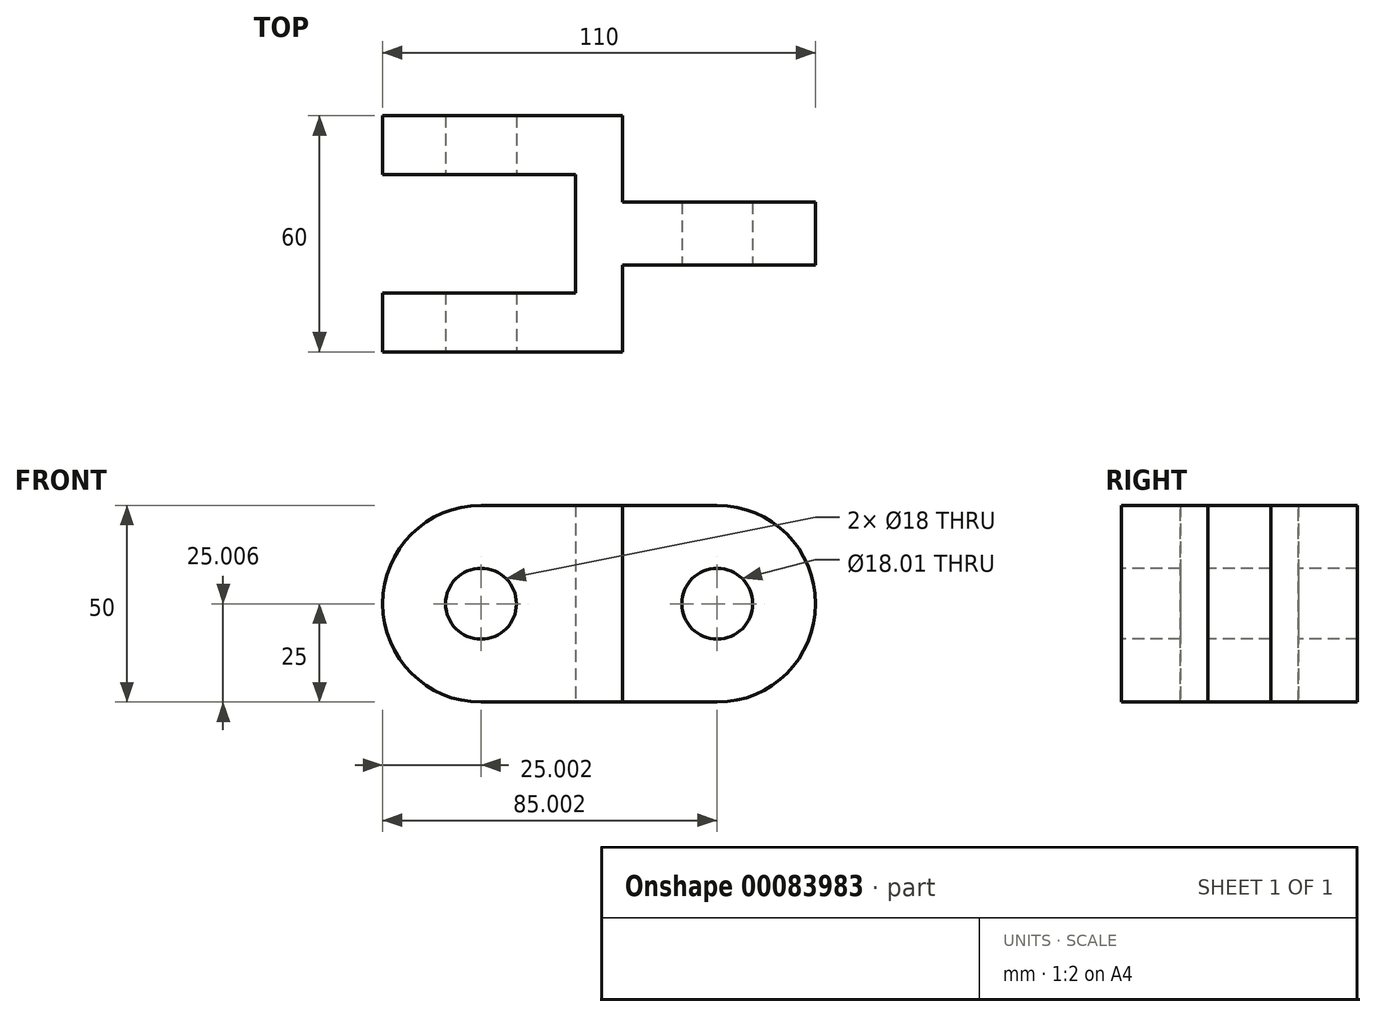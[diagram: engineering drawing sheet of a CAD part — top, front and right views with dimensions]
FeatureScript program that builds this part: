
annotation { "Feature Type Name" : "Feature", "Feature Type Description" : "" }
export const myFeature = defineFeature(function(context is Context, id is Id, definition is map)
    precondition{}
    {
        {
            var Q0;
            Q0=qCreatedBy(makeId("Top.planeOp"),FACE);
            var sketch = newSketch(context, id + "F0", { "sketchPlane" : qUnion([Q0])});
            skLineSegment(sketch, "E0.bottom", {"start": v(-55.44, 42.33) * mm, "end": v(54.56, 42.33) * mm});
            skLineSegment(sketch, "E0.top", {"start": v(-55.44, -17.67) * mm, "end": v(54.56, -17.67) * mm});
            skLineSegment(sketch, "E0.left", {"start": v(-55.44, 42.33) * mm, "end": v(-55.44, -17.67) * mm});
            skLineSegment(sketch, "E0.right", {"start": v(54.56, 42.33) * mm, "end": v(54.56, -17.67) * mm});
            skSolve(sketch);
        }
        {
            var Q0;
            Q0 = qSketchRegion(id + "F0", true);
            extrude(context, id + "F1", {"entities" : qUnion([Q0]), "depth" : 50 * mm});
        }
        {
            var Q0;
            Q0=qCreatedBy(makeId("Top.planeOp"),FACE);
            var sketch = newSketch(context, id + "F2", { "sketchPlane" : qUnion([Q0])});
            skLineSegment(sketch, "E1.bottom", {"start": v(54.56, -17.67) * mm, "end": v(5.56, -17.67) * mm});
            skLineSegment(sketch, "E1.top", {"start": v(54.56, 4.33) * mm, "end": v(5.56, 4.33) * mm});
            skLineSegment(sketch, "E1.left", {"start": v(54.56, -17.67) * mm, "end": v(54.56, 4.33) * mm});
            skLineSegment(sketch, "E1.right", {"start": v(5.56, -17.67) * mm, "end": v(5.56, 4.33) * mm});
            skLineSegment(sketch, "E2.bottom", {"start": v(54.56, 42.33) * mm, "end": v(5.57, 42.33) * mm});
            skLineSegment(sketch, "E2.top", {"start": v(54.56, 20.33) * mm, "end": v(5.57, 20.33) * mm});
            skLineSegment(sketch, "E2.left", {"start": v(54.56, 42.33) * mm, "end": v(54.56, 20.33) * mm});
            skLineSegment(sketch, "E2.right", {"start": v(5.57, 42.33) * mm, "end": v(5.57, 20.33) * mm});
            skLineSegment(sketch, "E3.bottom", {"start": v(-55.44, 27.33) * mm, "end": v(-6.44, 27.33) * mm});
            skLineSegment(sketch, "E3.top", {"start": v(-55.44, -2.67) * mm, "end": v(-6.44, -2.67) * mm});
            skLineSegment(sketch, "E3.left", {"start": v(-55.44, 27.33) * mm, "end": v(-55.44, -2.67) * mm});
            skLineSegment(sketch, "E3.right", {"start": v(-6.44, 27.33) * mm, "end": v(-6.44, -2.67) * mm});
            skSolve(sketch);
        }
        {
            var Q0;
            Q0 = qSketchRegion(id + "F2", true);
            extrude(context, id + "F3", {"entities" : qUnion([Q0]), "operationType" : NewBodyOperationType.REMOVE, "depth" : 50 * mm});
        }
        {
            var Q0;
            {var subQ0=sQuery(id+"F0.wireOp",EDGE,"E0.bottom");var subQ1=sQuery(id+"F0.wireOp",EDGE,"E0.left");Q0=makeQuery(id+"F3.boolean.opBoolean","SPLIT",EDGE,{"disambiguationData":[TD([makeQuery(id+"F1.opExtrude","SWEPT_FACE",FACE,{"disambiguationData":[OSD([subQ0])]})])],"derivedFrom":makeQuery(id+"F1.opExtrude","CAP_EDGE",EDGE,{"disambiguationData":[OSD([subQ1])],"isStart":false})});}
            var Q1;
            {var subQ0=sQuery(id+"F0.wireOp",EDGE,"E0.bottom");var subQ1=sQuery(id+"F0.wireOp",EDGE,"E0.left");Q1=makeQuery(id+"F3.boolean.opBoolean","SPLIT",EDGE,{"disambiguationData":[TD([makeQuery(id+"F1.opExtrude","SWEPT_FACE",FACE,{"disambiguationData":[OSD([subQ0])]})])],"derivedFrom":makeQuery(id+"F1.opExtrude","CAP_EDGE",EDGE,{"disambiguationData":[OSD([subQ1])],"isStart":true})});}
            var Q2;
            {var subQ0=sQuery(id+"F0.wireOp",EDGE,"E0.left");var subQ1=sQuery(id+"F0.wireOp",EDGE,"E0.top");Q2=makeQuery(id+"F3.boolean.opBoolean","SPLIT",EDGE,{"disambiguationData":[TD([makeQuery(id+"F1.opExtrude","SWEPT_FACE",FACE,{"disambiguationData":[OSD([subQ1])]})])],"derivedFrom":makeQuery(id+"F1.opExtrude","CAP_EDGE",EDGE,{"disambiguationData":[OSD([subQ0])],"isStart":false})});}
            var Q3;
            {var subQ0=sQuery(id+"F0.wireOp",EDGE,"E0.left");var subQ1=sQuery(id+"F0.wireOp",EDGE,"E0.top");Q3=makeQuery(id+"F3.boolean.opBoolean","SPLIT",EDGE,{"disambiguationData":[TD([makeQuery(id+"F1.opExtrude","SWEPT_FACE",FACE,{"disambiguationData":[OSD([subQ1])]})])],"derivedFrom":makeQuery(id+"F1.opExtrude","CAP_EDGE",EDGE,{"disambiguationData":[OSD([subQ0])],"isStart":true})});}
            var Q4;
            Q4=makeQuery(id+"F1.opExtrude","CAP_EDGE",EDGE,{"disambiguationData":[OSD([sQuery(id+"F0.wireOp",EDGE,"E0.right")])],"isStart":false});
            var Q5;
            Q5=makeQuery(id+"F1.opExtrude","CAP_EDGE",EDGE,{"disambiguationData":[OSD([sQuery(id+"F0.wireOp",EDGE,"E0.right")])],"isStart":true});
            fillet(context, id + "F4", {"entities" : qUnion([Q0, Q1, Q2, Q3, Q4, Q5]), "radius" : 25 * mm, "tangentPropagation" : true, "allowEdgeOverflow" : false});
        }
        {
            var Q0;
            Q0=qCreatedBy(makeId("Front.planeOp"),FACE);
            var sketch = newSketch(context, id + "F5", { "sketchPlane" : qUnion([Q0])});
            skCircle(sketch, "E4", {"center": v(-30.44, 25) * mm, "radius": 9 * mm});
            skCircle(sketch, "E5", {"center": v(29.56, 25) * mm, "radius": 9 * mm});
            skSolve(sketch);
        }
        {
            var Q0;
            Q0 = qSketchRegion(id + "F5", true);
            extrude(context, id + "F6", {"entities" : qUnion([Q0]), "operationType" : NewBodyOperationType.REMOVE, "endBound" : BoundingType.SYMMETRIC, "oppositeDirection" : true, "depth" : 50.16 * mm});
        }
        {
            var Q0;
            Q0 = qSketchRegion(id + "F5", true);
            extrude(context, id + "F7", {"entities" : qUnion([Q0]), "operationType" : NewBodyOperationType.REMOVE, "oppositeDirection" : true, "depth" : 58.26 * mm});
        }
    });
